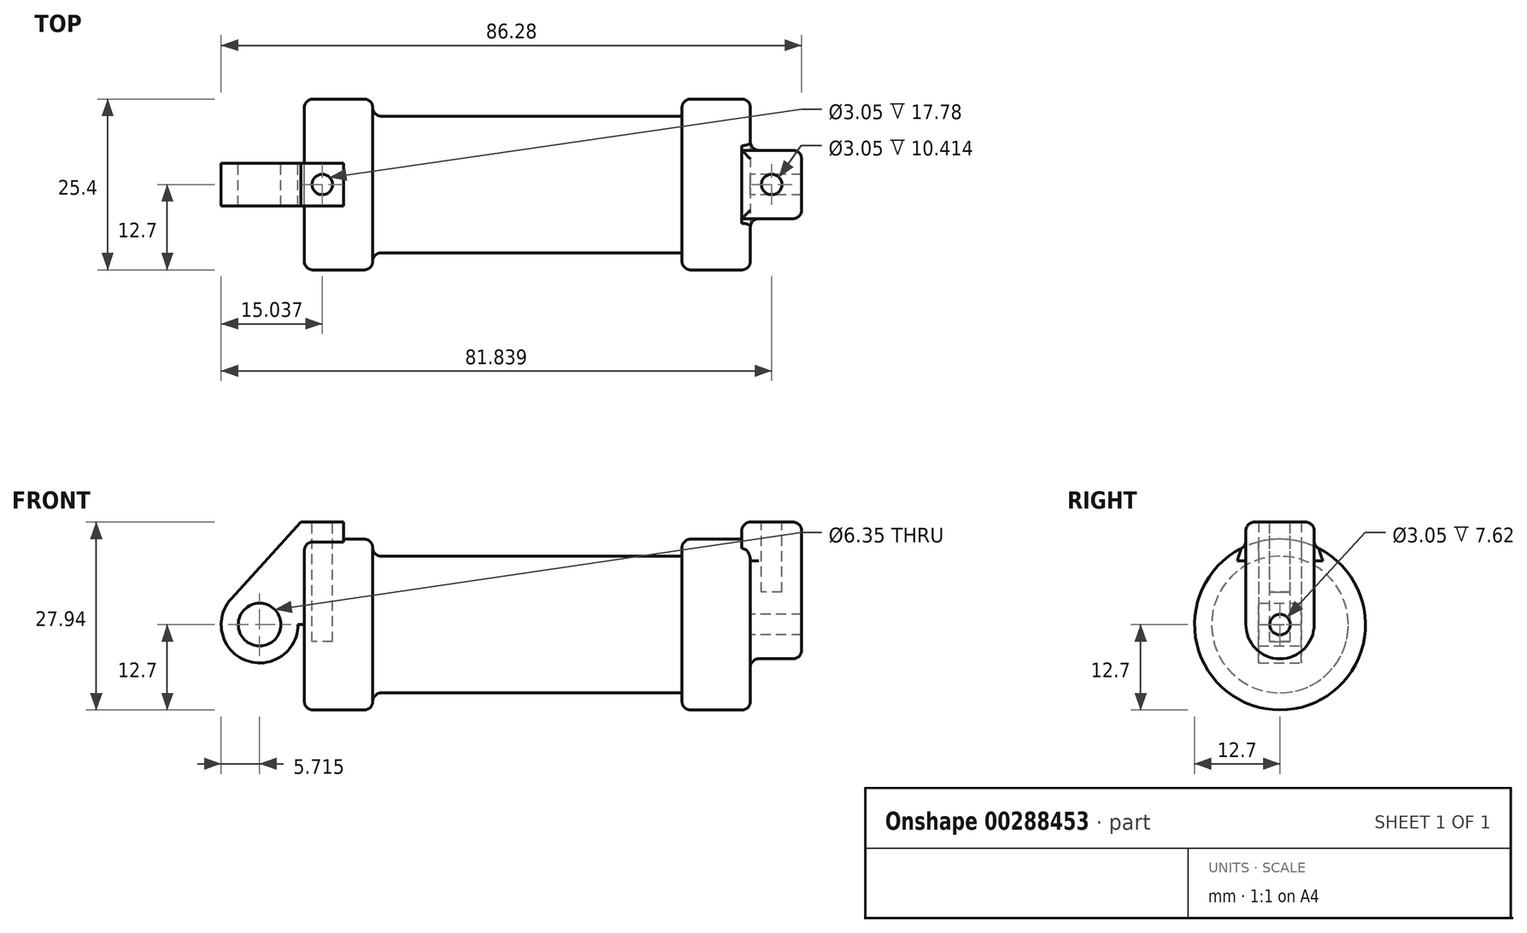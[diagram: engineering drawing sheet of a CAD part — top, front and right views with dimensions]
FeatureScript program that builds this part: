
annotation { "Feature Type Name" : "Feature", "Feature Type Description" : "" }
export const myFeature = defineFeature(function(context is Context, id is Id, definition is map)
    precondition{}
    {
        {
            var Q0;
            Q0=qCreatedBy(makeId("Front.planeOp"),FACE);
            var sketch = newSketch(context, id + "F0", { "sketchPlane" : qUnion([Q0])});
            skLineSegment(sketch, "E0", {"start": v(0, 0) * mm, "end": v(0, 12.7) * mm});
            skLineSegment(sketch, "E1", {"start": v(0, 12.7) * mm, "end": v(10.16, 12.7) * mm});
            skLineSegment(sketch, "E2", {"start": v(10.16, 12.7) * mm, "end": v(10.16, 10.16) * mm});
            skLineSegment(sketch, "E3", {"start": v(10.16, 10.16) * mm, "end": v(56.13, 10.16) * mm});
            skLineSegment(sketch, "E4", {"start": v(56.13, 10.16) * mm, "end": v(56.13, 12.7) * mm});
            skLineSegment(sketch, "E5", {"start": v(56.13, 12.7) * mm, "end": v(66.3, 12.7) * mm});
            skLineSegment(sketch, "E6", {"start": v(66.3, 12.7) * mm, "end": v(66.3, 0) * mm});
            skLineSegment(sketch, "E7", {"start": v(66.3, 0) * mm, "end": v(0, 0) * mm});
            skLineSegment(sketch, "E8", {"start": v(5.84, 15.24) * mm, "end": v(-0.5, 15.24) * mm});
            skLineSegment(sketch, "E9", {"start": v(-0.5, 15.24) * mm, "end": v(-10.88, 3.85) * mm});
            skLineSegment(sketch, "E10", {"start": v(0, 0) * mm, "end": v(-6.65, 0) * mm});
            skCircle(sketch, "E11", {"center": v(-6.65, 0) * mm, "radius": 5.72 * mm});
            skCircle(sketch, "E12", {"center": v(-6.65, 0) * mm, "radius": 3.18 * mm});
            skLineSegment(sketch, "E13", {"start": v(5.84, 15.24) * mm, "end": v(5.84, -9.4) * mm});
            skLineSegment(sketch, "E14", {"start": v(5.84, -9.4) * mm, "end": v(-8.18, -5.5) * mm});
            skSolve(sketch);
        }
        {
            var Q0;
            {var subQ0=sQuery(id+"F0.wireOp",EDGE,"E2");Q0=makeQuery(id+"F0.imprint","IMPRINT",FACE,{"disambiguationData":[TD([[makeQuery(id+"F0.imprint","IMPRINT",EDGE,{"derivedFrom":subQ0}),-1.0]])]});}
            var Q1;
            {var subQ0=sQuery(id+"F0.wireOp",EDGE,"E0");Q1=makeQuery(id+"F0.imprint","IMPRINT",FACE,{"disambiguationData":[TD([[makeQuery(id+"F0.imprint","IMPRINT",EDGE,{"derivedFrom":subQ0}),-1.0]])]});}
            var Q2;
            Q2=sQuery(id+"F0.wireOp",EDGE,"E10");
            revolve(context, id + "F1", {"entities" : qUnion([Q0, Q1]), "axis" : qUnion([Q2]), "revolveType" : RevolveType.FULL});
        }
        {
            var Q0;
            {var subQ1=sQuery(id+"F0.wireOp",EDGE,"E0");Q0=makeQuery(id+"F0.imprint","IMPRINT",FACE,{"disambiguationData":[TD([[makeQuery(id+"F0.imprint","IMPRINT",EDGE,{"derivedFrom":subQ1}),1.0]])]});}
            var Q1;
            {var subQ0=sQuery(id+"F0.wireOp",EDGE,"E0");Q1=makeQuery(id+"F0.imprint","IMPRINT",FACE,{"disambiguationData":[TD([[makeQuery(id+"F0.imprint","IMPRINT",EDGE,{"derivedFrom":subQ0}),-1.0]])]});}
            var Q2;
            {var subQ5=sQuery(id+"F0.wireOp",EDGE,"E12");Q2=makeQuery(id+"F0.imprint","IMPRINT",FACE,{"disambiguationData":[TD([[makeQuery(id+"F0.imprint","IMPRINT",EDGE,{"derivedFrom":subQ5}),-1.0]])]});}
            extrude(context, id + "F2", {"entities" : qUnion([Q0, Q1, Q2]), "operationType" : NewBodyOperationType.ADD, "endBound" : BoundingType.SYMMETRIC, "depth" : 6.35 * mm});
        }
        {
            var Q0;
            Q0=makeQuery(id+"F1.opRevolve","SWEPT_FACE",FACE,{"disambiguationData":[OSD([sQuery(id+"F0.wireOp",EDGE,"E6")])]});
            var sketch = newSketch(context, id + "F3", { "sketchPlane" : qUnion([Q0])});
            skCircle(sketch, "E15", {"center": v(0, 0) * mm, "radius": 5.08 * mm});
            skCircle(sketch, "E16", {"center": v(0, 0) * mm, "radius": 1.52 * mm});
            skLineSegment(sketch, "E17", {"start": v(5.08, 0) * mm, "end": v(5.08, 15.24) * mm});
            skLineSegment(sketch, "E18", {"start": v(5.08, 15.24) * mm, "end": v(-5.08, 15.24) * mm});
            skLineSegment(sketch, "E19", {"start": v(-5.08, 15.24) * mm, "end": v(-5.08, 0) * mm});
            skSolve(sketch);
        }
        {
            var Q0;
            {var subQ0=sQuery(id+"F3.wireOp",EDGE,"E18");Q0=makeQuery(id+"F3.imprint","IMPRINT",FACE,{"disambiguationData":[TD([[makeQuery(id+"F3.imprint","IMPRINT",EDGE,{"derivedFrom":subQ0}),1.0]])]});}
            var Q1;
            {var subQ0=sQuery(id+"F3.wireOp",EDGE,"E17");var subQ1=sQuery(id+"F3.wireOp",EDGE,"E15");var subQ2=makeQuery(id+"F3.imprint","INTERSECT",VERTEX,{"derivedFrom":[subQ1,subQ0]});Q1=makeQuery(id+"F3.imprint","IMPRINT",FACE,{"disambiguationData":[TD([[makeQuery(id+"F3.imprint","IMPRINT",EDGE,{"disambiguationData":[TD([[subQ2,-1.0]])],"derivedFrom":subQ1}),-1.0]])]});}
            var Q2;
            Q2=makeQuery(id+"F3.imprint","IMPRINT",FACE,{"disambiguationData":[TD([[makeQuery(id+"F3.imprint","IMPRINT",EDGE,{"derivedFrom":sQuery(id+"F3.wireOp",EDGE,"E16")}),-1.0]])]});
            extrude(context, id + "F4", {"entities" : qUnion([Q0, Q1, Q2]), "operationType" : NewBodyOperationType.ADD, "depth" : 7.62 * mm});
        }
        {
            var Q0;
            Q0=makeQuery(id+"F4.opExtrude","CAP_FACE",FACE,{"disambiguationData":[OSD([sQuery(id+"F3.wireOp",EDGE,"E15"),sQuery(id+"F3.wireOp",EDGE,"E16"),sQuery(id+"F3.wireOp",EDGE,"E17"),sQuery(id+"F3.wireOp",EDGE,"E18"),sQuery(id+"F3.wireOp",EDGE,"E19")])],"isStart":true});
            extrude(context, id + "F5", {"entities" : qUnion([Q0]), "operationType" : NewBodyOperationType.ADD, "depth" : 1.27 * mm});
        }
        {
            var Q0;
            {var subQ0=sQuery(id+"F3.wireOp",EDGE,"E18");Q0=makeQuery(id+"F5.boolean.opBoolean","MERGE",FACE,{"derivedFrom":[makeQuery(id+"F4.opExtrude","SWEPT_FACE",FACE,{"disambiguationData":[OSD([subQ0])]}),makeQuery(id+"F5.opExtrude","SWEPT_FACE",FACE,{"disambiguationData":[OSD([subQ0])]})]});}
            var sketch = newSketch(context, id + "F6", { "sketchPlane" : qUnion([Q0])});
            skPoint(sketch, "E20.0", {"position": v(69.47, 5.08) * mm});
            skPoint(sketch, "E21.0", {"position": v(65.02, 0) * mm});
            skCircle(sketch, "E22", {"center": v(69.47, 0) * mm, "radius": 1.52 * mm});
            skSolve(sketch);
        }
        {
            var Q0;
            Q0=makeQuery(id+"F2.opExtrude","SWEPT_FACE",FACE,{"disambiguationData":[OSD([sQuery(id+"F0.wireOp",EDGE,"E8")])]});
            var sketch = newSketch(context, id + "F7", { "sketchPlane" : qUnion([Q0])});
            skPoint(sketch, "E23", {"position": v(2.67, 3.18) * mm});
            skPoint(sketch, "E24", {"position": v(5.84, 0) * mm});
            skCircle(sketch, "E25", {"center": v(2.67, 0) * mm, "radius": 1.52 * mm});
            skSolve(sketch);
        }
        {
            var Q0;
            Q0=makeQuery(id+"F7.imprint","IMPRINT",FACE,{"disambiguationData":[TD([[makeQuery(id+"F7.imprint","IMPRINT",EDGE,{"derivedFrom":sQuery(id+"F7.wireOp",EDGE,"E25")}),1.0]])]});
            extrude(context, id + "F8", {"entities" : qUnion([Q0]), "operationType" : NewBodyOperationType.REMOVE, "oppositeDirection" : true, "depth" : 17.78 * mm});
        }
        {
            var Q0;
            Q0=makeQuery(id+"F6.imprint","IMPRINT",FACE,{"disambiguationData":[TD([[makeQuery(id+"F6.imprint","IMPRINT",EDGE,{"derivedFrom":sQuery(id+"F6.wireOp",EDGE,"E22")}),1.0]])]});
            var Q1;
            Q1=sQuery(id+"F6.wireOp",EDGE,"E22");
            extrude(context, id + "F9", {"entities" : qUnion([Q0]), "operationType" : NewBodyOperationType.REMOVE, "surfaceEntities" : qUnion([Q1]), "oppositeDirection" : true, "depth" : 10.4 * mm});
        }
        {
            var Q0;
            {var subQ0=sQuery(id+"F0.wireOp",EDGE,"E5");var subQ1=sQuery(id+"F0.wireOp",EDGE,"E6");Q0=makeQuery(id+"F4.boolean.opBoolean","SPLIT",EDGE,{"disambiguationData":[topologyDisambiguationEdgeConnected([makeQuery(id+"F1.opRevolve","SWEPT_FACE",FACE,{"disambiguationData":[OSD([subQ1])]})])],"derivedFrom":makeQuery(id+"F1.opRevolve","SWEPT_EDGE",EDGE,{"disambiguationData":[OSD([subQ0,subQ1])]})});}
            var Q1;
            Q1=makeQuery(id+"F1.opRevolve","SWEPT_EDGE",EDGE,{"disambiguationData":[OSD([sQuery(id+"F0.wireOp",EDGE,"E4"),sQuery(id+"F0.wireOp",EDGE,"E5")])]});
            var Q2;
            Q2=makeQuery(id+"F1.opRevolve","SWEPT_EDGE",EDGE,{"disambiguationData":[OSD([sQuery(id+"F0.wireOp",EDGE,"E1"),sQuery(id+"F0.wireOp",EDGE,"E2")])]});
            var Q3;
            Q3=makeQuery(id+"F1.opRevolve","SWEPT_EDGE",EDGE,{"disambiguationData":[OSD([sQuery(id+"F0.wireOp",EDGE,"E0"),sQuery(id+"F0.wireOp",EDGE,"E1")])]});
            var Q4;
            Q4=makeQuery(id+"F1.opRevolve","SWEPT_EDGE",EDGE,{"disambiguationData":[OSD([sQuery(id+"F0.wireOp",EDGE,"E2"),sQuery(id+"F0.wireOp",EDGE,"E3")])]});
            fillet(context, id + "F10", {"entities" : qUnion([Q0, Q1, Q2, Q3, Q4]), "radius" : 1.27 * mm, "tangentPropagation" : true, "allowEdgeOverflow" : false});
        }
        {
            var Q0;
            Q0=makeQuery(id+"F4.opExtrude","CAP_EDGE",EDGE,{"disambiguationData":[OSD([sQuery(id+"F3.wireOp",EDGE,"E19")])],"isStart":false});
            var Q1;
            Q1=makeQuery(id+"F4.boolean.opBoolean","SPLIT",FACE,{"disambiguationData":[TD([makeQuery(id+"F1.opRevolve","SWEPT_FACE",FACE,{"disambiguationData":[OSD([sQuery(id+"F0.wireOp",EDGE,"E5")])]})])],"derivedFrom":makeQuery(id+"F1.opRevolve","SWEPT_FACE",FACE,{"disambiguationData":[OSD([sQuery(id+"F0.wireOp",EDGE,"E6")])]})});
            var Q2;
            {var subQ0=sQuery(id+"F3.wireOp",EDGE,"E18");var subQ1=sQuery(id+"F3.wireOp",EDGE,"E17");Q2=makeQuery(id+"F5.boolean.opBoolean","MERGE",EDGE,{"derivedFrom":[makeQuery(id+"F4.opExtrude","SWEPT_EDGE",EDGE,{"disambiguationData":[OSD([subQ1,subQ0])]}),makeQuery(id+"F5.opExtrude","SWEPT_EDGE",EDGE,{"disambiguationData":[OSD([subQ1,subQ0])]})]});}
            var Q3;
            {var subQ0=sQuery(id+"F3.wireOp",EDGE,"E19");var subQ1=sQuery(id+"F3.wireOp",EDGE,"E18");Q3=makeQuery(id+"F5.boolean.opBoolean","MERGE",EDGE,{"derivedFrom":[makeQuery(id+"F4.opExtrude","SWEPT_EDGE",EDGE,{"disambiguationData":[OSD([subQ1,subQ0])]}),makeQuery(id+"F5.opExtrude","SWEPT_EDGE",EDGE,{"disambiguationData":[OSD([subQ1,subQ0])]})]});}
            var Q4;
            Q4=makeQuery(id+"F4.opExtrude","CAP_EDGE",EDGE,{"disambiguationData":[OSD([sQuery(id+"F3.wireOp",EDGE,"E18")])],"isStart":false});
            var Q5;
            Q5=makeQuery(id+"F5.opExtrude","CAP_EDGE",EDGE,{"disambiguationData":[OSD([sQuery(id+"F3.wireOp",EDGE,"E18")])],"isStart":false});
            var Q6;
            Q6=makeQuery(id+"F5.opExtrude","CAP_EDGE",EDGE,{"disambiguationData":[OSD([sQuery(id+"F0.wireOp",EDGE,"E5"),sQuery(id+"F0.wireOp",EDGE,"E6")])],"isStart":false});
            fillet(context, id + "F11", {"entities" : qUnion([Q0, Q1, Q2, Q3, Q4, Q5, Q6]), "radius" : 1.27 * mm, "tangentPropagation" : true, "allowEdgeOverflow" : false});
        }
    });
